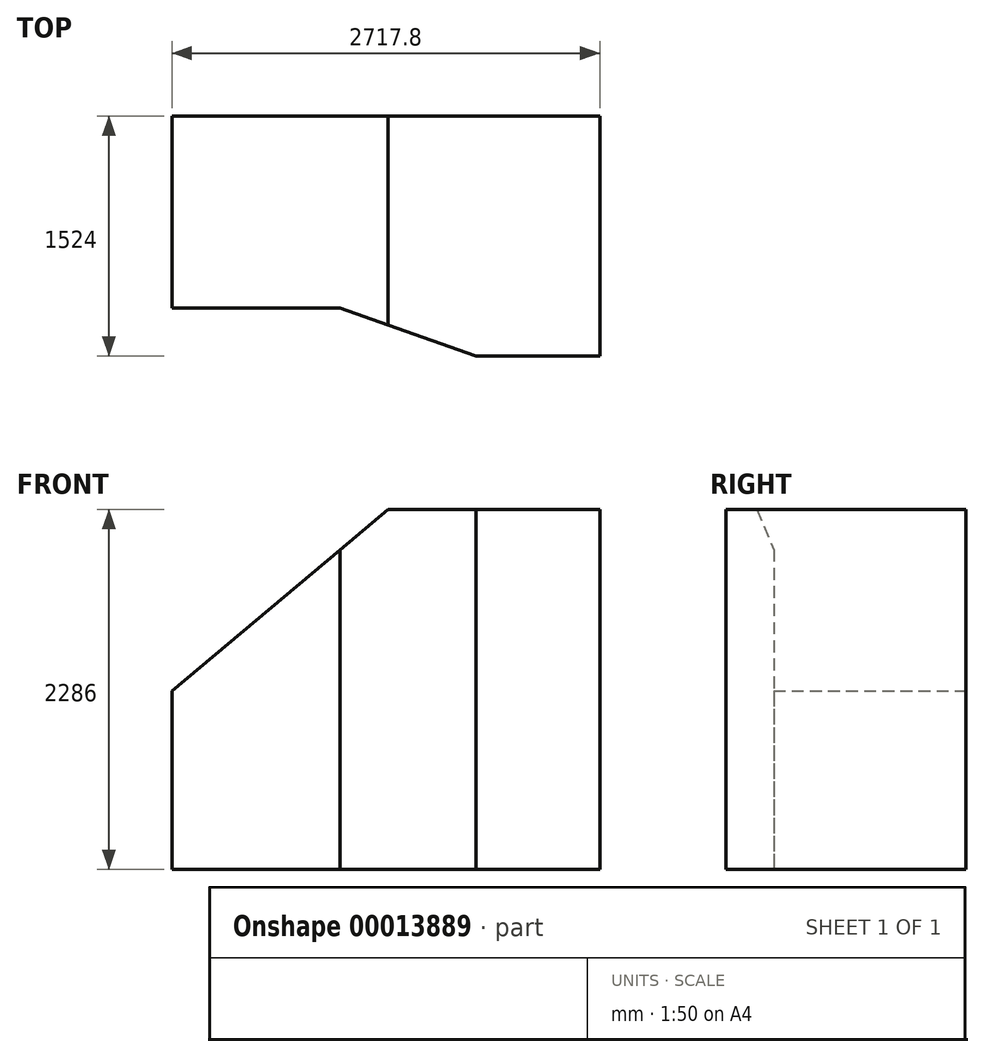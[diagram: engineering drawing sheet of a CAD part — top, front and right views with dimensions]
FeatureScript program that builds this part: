
annotation { "Feature Type Name" : "Feature", "Feature Type Description" : "" }
export const myFeature = defineFeature(function(context is Context, id is Id, definition is map)
    precondition{}
    {
        {
            var Q0;
            Q0=qCreatedBy(makeId("Front.planeOp"),FACE);
            var sketch = newSketch(context, id + "F0", { "sketchPlane" : qUnion([Q0])});
            skLineSegment(sketch, "E0", {"start": v(-4483.36, 0) * mm, "end": v(-850.9, 3048) * mm});
            skSolve(sketch);
        }
        {
            var Q0;
            Q0=sQuery(id+"F0.wireOp",EDGE,"E0");
            extrude(context, id + "F1", {"bodyType" : ToolBodyType.SURFACE, "surfaceEntities" : qUnion([Q0]), "depth" : 812.8 * mm});
        }
        {
            var Q0;
            Q0=qCreatedBy(makeId("Front.planeOp"),FACE);
            cPlane(context, id + "F2", {"entities" : qUnion([Q0]), "cplaneType" : CPlaneType.OFFSET, "offset" : 2438.4 * mm, "width" : 152.4 * mm, "height" : 152.4 * mm});
        }
        {
            var Q0;
            Q0=qCreatedBy(makeId("Front.planeOp"),FACE);
            var sketch = newSketch(context, id + "F3", { "sketchPlane" : qUnion([Q0])});
            skLineSegment(sketch, "E1", {"start": v(-2895.6, 0) * mm, "end": v(-2895.6, 1133.35) * mm});
            skLineSegment(sketch, "E2", {"start": v(-2895.6, 1133.35) * mm, "end": v(-1521.92, 2286) * mm});
            skLineSegment(sketch, "E3", {"start": v(-1521.92, 2286) * mm, "end": v(-203.2, 2286) * mm});
            skLineSegment(sketch, "E4", {"start": v(-203.2, 2286) * mm, "end": v(-203.2, 0) * mm});
            skLineSegment(sketch, "E5", {"start": v(-203.2, 0) * mm, "end": v(-2895.6, 0) * mm});
            skSolve(sketch);
        }
        {
            var Q0;
            Q0=makeQuery(id+"F3.imprint","IMPRINT",FACE,{"disambiguationData":[TD([[makeQuery(id+"F3.imprint","IMPRINT",EDGE,{"derivedFrom":sQuery(id+"F3.wireOp",EDGE,"E1")}),-1.0]])]});
            extrude(context, id + "F4", {"entities" : qUnion([Q0]), "depth" : 1524 * mm});
        }
        {
            var Q0;
            Q0=makeQuery(id+"F4.opExtrude","SWEPT_FACE",FACE,{"disambiguationData":[OSD([sQuery(id+"F3.wireOp",EDGE,"E5")])]});
            var sketch = newSketch(context, id + "F5", { "sketchPlane" : qUnion([Q0])});
            skLineSegment(sketch, "E6", {"start": v(-203.2, 1524) * mm, "end": v(-965.2, 1524) * mm});
            skLineSegment(sketch, "E7", {"start": v(-965.2, 1524) * mm, "end": v(-1827.3, 1219.2) * mm});
            skLineSegment(sketch, "E8", {"start": v(-1827.3, 1219.2) * mm, "end": v(-2895.6, 1219.2) * mm});
            skLineSegment(sketch, "E9", {"start": v(-2895.6, 1219.2) * mm, "end": v(-2895.6, 1524) * mm});
            skLineSegment(sketch, "E10", {"start": v(-2895.6, 1524) * mm, "end": v(-965.2, 1524) * mm});
            skSolve(sketch);
        }
        {
            var Q0;
            Q0=makeQuery(id+"F5.imprint","IMPRINT",FACE,{"disambiguationData":[TD([[makeQuery(id+"F5.imprint","IMPRINT",EDGE,{"derivedFrom":sQuery(id+"F5.wireOp",EDGE,"E7")}),-1.0]])]});
            extrude(context, id + "F6", {"entities" : qUnion([Q0]), "operationType" : NewBodyOperationType.REMOVE, "endBound" : BoundingType.UP_TO_NEXT, "oppositeDirection" : true, "depth" : 25.4 * mm});
        }
        {
            var Q0;
            Q0=makeQuery(id+"F4.opExtrude","SWEPT_FACE",FACE,{"disambiguationData":[OSD([sQuery(id+"F3.wireOp",EDGE,"E4")])]});
            extrude(context, id + "F7", {"entities" : qUnion([Q0]), "operationType" : NewBodyOperationType.ADD, "depth" : 25.4 * mm});
        }
    });
